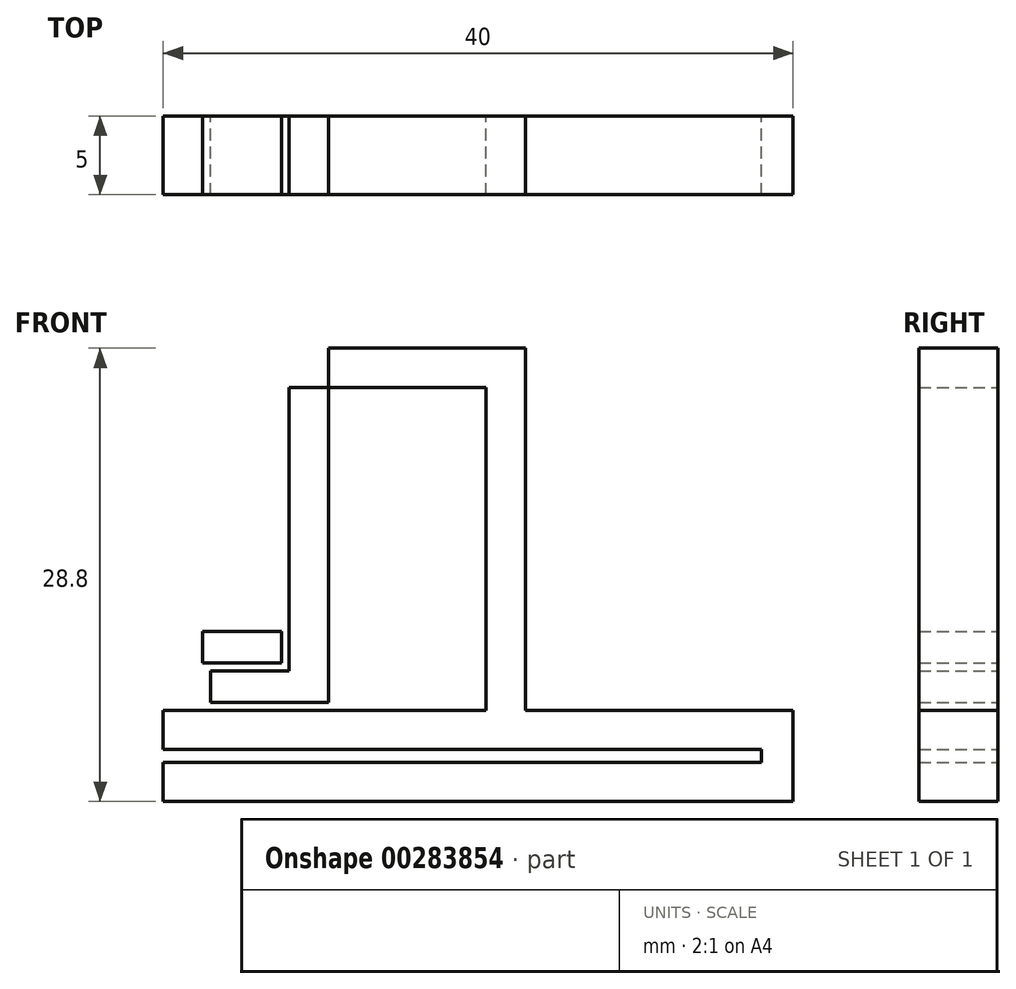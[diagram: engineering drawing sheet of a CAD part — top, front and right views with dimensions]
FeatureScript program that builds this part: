
annotation { "Feature Type Name" : "Feature", "Feature Type Description" : "" }
export const myFeature = defineFeature(function(context is Context, id is Id, definition is map)
    precondition{}
    {
        {
            var Q0;
            Q0=qCreatedBy(makeId("Front.planeOp"),FACE);
            var sketch = newSketch(context, id + "F0", { "sketchPlane" : qUnion([Q0])});
            skLineSegment(sketch, "E0.bottom", {"start": v(-20, -0.4) * mm, "end": v(20, -0.4) * mm, "construction": true});
            skLineSegment(sketch, "E0.top", {"start": v(-20, 0.4) * mm, "end": v(20, 0.4) * mm, "construction": true});
            skLineSegment(sketch, "E0.left", {"start": v(-20, -0.4) * mm, "end": v(-20, 0.4) * mm, "construction": true});
            skLineSegment(sketch, "E0.right", {"start": v(20, -0.4) * mm, "end": v(20, 0.4) * mm, "construction": true});
            skPoint(sketch, "E0.middle", {"position": v(0, 0) * mm});
            skLineSegment(sketch, "E1", {"start": v(-20, 0) * mm, "end": v(20, 0) * mm, "construction": true});
            skLineSegment(sketch, "E2.bottom", {"start": v(-20, -0.4) * mm, "end": v(20, -0.4) * mm});
            skLineSegment(sketch, "E2.top", {"start": v(-20, -2.9) * mm, "end": v(20, -2.9) * mm});
            skLineSegment(sketch, "E2.left", {"start": v(-20, -0.4) * mm, "end": v(-20, -2.9) * mm});
            skLineSegment(sketch, "E2.right", {"start": v(20, -0.4) * mm, "end": v(20, -2.9) * mm});
            skLineSegment(sketch, "E3.bottom", {"start": v(20, 0) * mm, "end": v(18, 0) * mm});
            skLineSegment(sketch, "E3.top", {"start": v(20, -2.9) * mm, "end": v(18, -2.9) * mm});
            skLineSegment(sketch, "E3.left", {"start": v(20, 0) * mm, "end": v(20, -2.9) * mm});
            skLineSegment(sketch, "E3.right", {"start": v(18, 0) * mm, "end": v(18, -2.9) * mm});
            skLineSegment(sketch, "E4.MirrorCS", {"start": v(-20, 0.4) * mm, "end": v(20, 0.4) * mm});
            skLineSegment(sketch, "E5.MirrorCS", {"start": v(-20, 0.4) * mm, "end": v(-20, 2.9) * mm});
            skLineSegment(sketch, "E6.MirrorCS", {"start": v(-20, 2.9) * mm, "end": v(20, 2.9) * mm});
            skLineSegment(sketch, "E7.MirrorCS", {"start": v(20, 0) * mm, "end": v(20, 2.9) * mm});
            skLineSegment(sketch, "E8.MirrorCS", {"start": v(18, 0) * mm, "end": v(18, 2.9) * mm});
            skLineSegment(sketch, "E9.bottom", {"start": v(-20, 2.9) * mm, "end": v(-17.5, 2.9) * mm});
            skLineSegment(sketch, "E9.top", {"start": v(-20, 7.9) * mm, "end": v(-17.5, 7.9) * mm});
            skLineSegment(sketch, "E9.left", {"start": v(-20, 2.9) * mm, "end": v(-20, 7.9) * mm});
            skLineSegment(sketch, "E9.right", {"start": v(-17.5, 2.9) * mm, "end": v(-17.5, 7.9) * mm});
            skLineSegment(sketch, "E10.bottom", {"start": v(-17.5, 7.9) * mm, "end": v(-12.5, 7.9) * mm});
            skLineSegment(sketch, "E10.top", {"start": v(-17.5, 5.9) * mm, "end": v(-12.5, 5.9) * mm});
            skLineSegment(sketch, "E10.left", {"start": v(-17.5, 7.9) * mm, "end": v(-17.5, 5.9) * mm});
            skLineSegment(sketch, "E10.right", {"start": v(-12.5, 7.9) * mm, "end": v(-12.5, 5.9) * mm});
            skLineSegment(sketch, "E11.bottom", {"start": v(-17.5, 2.9) * mm, "end": v(-17, 2.9) * mm, "construction": true});
            skLineSegment(sketch, "E11.top", {"start": v(-17.5, 3.4) * mm, "end": v(-17, 3.4) * mm, "construction": true});
            skLineSegment(sketch, "E11.left", {"start": v(-17.5, 2.9) * mm, "end": v(-17.5, 3.4) * mm, "construction": true});
            skLineSegment(sketch, "E11.right", {"start": v(-17, 2.9) * mm, "end": v(-17, 3.4) * mm, "construction": true});
            skLineSegment(sketch, "E12.bottom", {"start": v(-12.5, 5.9) * mm, "end": v(-12, 5.9) * mm, "construction": true});
            skLineSegment(sketch, "E12.top", {"start": v(-12.5, 5.4) * mm, "end": v(-12, 5.4) * mm, "construction": true});
            skLineSegment(sketch, "E12.left", {"start": v(-12.5, 5.9) * mm, "end": v(-12.5, 5.4) * mm, "construction": true});
            skLineSegment(sketch, "E12.right", {"start": v(-12, 5.9) * mm, "end": v(-12, 5.4) * mm, "construction": true});
            skLineSegment(sketch, "E13.bottom", {"start": v(-17, 3.4) * mm, "end": v(-12, 3.4) * mm});
            skLineSegment(sketch, "E13.top", {"start": v(-17, 5.4) * mm, "end": v(-12, 5.4) * mm});
            skLineSegment(sketch, "E13.left", {"start": v(-17, 3.4) * mm, "end": v(-17, 5.4) * mm});
            skLineSegment(sketch, "E13.right", {"start": v(-12, 3.4) * mm, "end": v(-12, 5.4) * mm});
            skLineSegment(sketch, "E14.bottom", {"start": v(-12, 3.4) * mm, "end": v(-9.5, 3.4) * mm});
            skLineSegment(sketch, "E14.top", {"start": v(-12, 23.4) * mm, "end": v(-9.5, 23.4) * mm});
            skLineSegment(sketch, "E14.left", {"start": v(-12, 3.4) * mm, "end": v(-12, 23.4) * mm});
            skLineSegment(sketch, "E14.right", {"start": v(-9.5, 3.4) * mm, "end": v(-9.5, 23.4) * mm});
            skLineSegment(sketch, "E15.bottom", {"start": v(-9.5, 23.4) * mm, "end": v(0.5, 23.4) * mm});
            skLineSegment(sketch, "E15.top", {"start": v(-9.5, 25.9) * mm, "end": v(0.5, 25.9) * mm});
            skLineSegment(sketch, "E15.left", {"start": v(-9.5, 23.4) * mm, "end": v(-9.5, 25.9) * mm});
            skLineSegment(sketch, "E15.right", {"start": v(0.5, 23.4) * mm, "end": v(0.5, 25.9) * mm});
            skLineSegment(sketch, "E16.bottom", {"start": v(-9.5, 23.4) * mm, "end": v(-12, 23.4) * mm});
            skLineSegment(sketch, "E16.top", {"start": v(-9.5, 25.9) * mm, "end": v(-12, 25.9) * mm});
            skLineSegment(sketch, "E16.right", {"start": v(-12, 23.4) * mm, "end": v(-12, 25.9) * mm});
            skLineSegment(sketch, "E17.bottom", {"start": v(0.5, 25.9) * mm, "end": v(3, 25.9) * mm});
            skLineSegment(sketch, "E17.top", {"start": v(0.5, 2.9) * mm, "end": v(3, 2.9) * mm});
            skLineSegment(sketch, "E17.left", {"start": v(0.5, 25.9) * mm, "end": v(0.5, 2.9) * mm});
            skLineSegment(sketch, "E17.right", {"start": v(3, 25.9) * mm, "end": v(3, 2.9) * mm});
            skSolve(sketch);
        }
        {
            var Q0;
            {var subQ4=sQuery(id+"F0.wireOp",EDGE,"E2.top");Q0=makeQuery(id+"F0.imprint","IMPRINT",FACE,{"disambiguationData":[TD([[makeQuery(id+"F0.imprint","IMPRINT",EDGE,{"derivedFrom":subQ4}),1.0]])]});}
            var Q1;
            {var subQ5=sQuery(id+"F0.wireOp",EDGE,"E3.top");Q1=makeQuery(id+"F0.imprint","IMPRINT",FACE,{"disambiguationData":[TD([[makeQuery(id+"F0.imprint","IMPRINT",EDGE,{"derivedFrom":subQ5}),-1.0]])]});}
            var Q2;
            {var subQ5=sQuery(id+"F0.wireOp",EDGE,"E3.bottom");Q2=makeQuery(id+"F0.imprint","IMPRINT",FACE,{"disambiguationData":[TD([[makeQuery(id+"F0.imprint","IMPRINT",EDGE,{"derivedFrom":subQ5}),1.0]])]});}
            var Q3;
            {var subQ5=sQuery(id+"F0.wireOp",EDGE,"E3.bottom");Q3=makeQuery(id+"F0.imprint","IMPRINT",FACE,{"disambiguationData":[TD([[makeQuery(id+"F0.imprint","IMPRINT",EDGE,{"derivedFrom":subQ5}),-1.0]])]});}
            var Q4;
            {var subQ0=sQuery(id+"F0.wireOp",EDGE,"E7.MirrorCS");var subQ1=sQuery(id+"F0.wireOp",EDGE,"E4.MirrorCS");var subQ2=makeQuery(id+"F0.imprint","INTERSECT",VERTEX,{"derivedFrom":[subQ1,subQ0]});Q4=makeQuery(id+"F0.imprint","IMPRINT",FACE,{"disambiguationData":[TD([[makeQuery(id+"F0.imprint","IMPRINT",EDGE,{"disambiguationData":[TD([[subQ2,1.0]])],"derivedFrom":subQ1}),1.0]])]});}
            var Q5;
            {var subQ5=sQuery(id+"F0.wireOp",EDGE,"E5.MirrorCS");Q5=makeQuery(id+"F0.imprint","IMPRINT",FACE,{"disambiguationData":[TD([[makeQuery(id+"F0.imprint","IMPRINT",EDGE,{"derivedFrom":subQ5}),-1.0]])]});}
            var Q6;
            {var subQ3=sQuery(id+"F0.wireOp",EDGE,"E17.bottom");Q6=makeQuery(id+"F0.imprint","IMPRINT",FACE,{"disambiguationData":[TD([[makeQuery(id+"F0.imprint","IMPRINT",EDGE,{"derivedFrom":subQ3}),-1.0]])]});}
            var Q7;
            {var subQ0=sQuery(id+"F0.wireOp",EDGE,"E15.bottom");Q7=makeQuery(id+"F0.imprint","IMPRINT",FACE,{"disambiguationData":[TD([[makeQuery(id+"F0.imprint","IMPRINT",EDGE,{"derivedFrom":subQ0}),1.0]])]});}
            var Q8;
            Q8=makeQuery(id+"F0.imprint","IMPRINT",FACE,{"disambiguationData":[TD([[makeQuery(id+"F0.imprint","IMPRINT",EDGE,{"derivedFrom":sQuery(id+"F0.wireOp",EDGE,"E16.bottom")}),-1.0]])]});
            var Q9;
            {var subQ3=sQuery(id+"F0.wireOp",EDGE,"E14.bottom");Q9=makeQuery(id+"F0.imprint","IMPRINT",FACE,{"disambiguationData":[TD([[makeQuery(id+"F0.imprint","IMPRINT",EDGE,{"derivedFrom":subQ3}),1.0]])]});}
            var Q10;
            {var subQ0=sQuery(id+"F0.wireOp",EDGE,"E13.bottom");Q10=makeQuery(id+"F0.imprint","IMPRINT",FACE,{"disambiguationData":[TD([[makeQuery(id+"F0.imprint","IMPRINT",EDGE,{"derivedFrom":subQ0}),1.0]])]});}
            var Q11;
            Q11=makeQuery(id+"F0.imprint","IMPRINT",FACE,{"disambiguationData":[TD([[makeQuery(id+"F0.imprint","IMPRINT",EDGE,{"derivedFrom":sQuery(id+"F0.wireOp",EDGE,"E10.bottom")}),-1.0]])]});
            var Q12;
            Q12=makeQuery(id+"F0.imprint","IMPRINT",FACE,{"disambiguationData":[TD([[makeQuery(id+"F0.imprint","IMPRINT",EDGE,{"derivedFrom":sQuery(id+"F0.wireOp",EDGE,"E9.bottom")}),1.0]])]});
            extrude(context, id + "F1", {"entities" : qUnion([Q0, Q1, Q2, Q3, Q4, Q5, Q6, Q7, Q8, Q9, Q10, Q11, Q12]), "depth" : 5 * mm});
        }
    });
